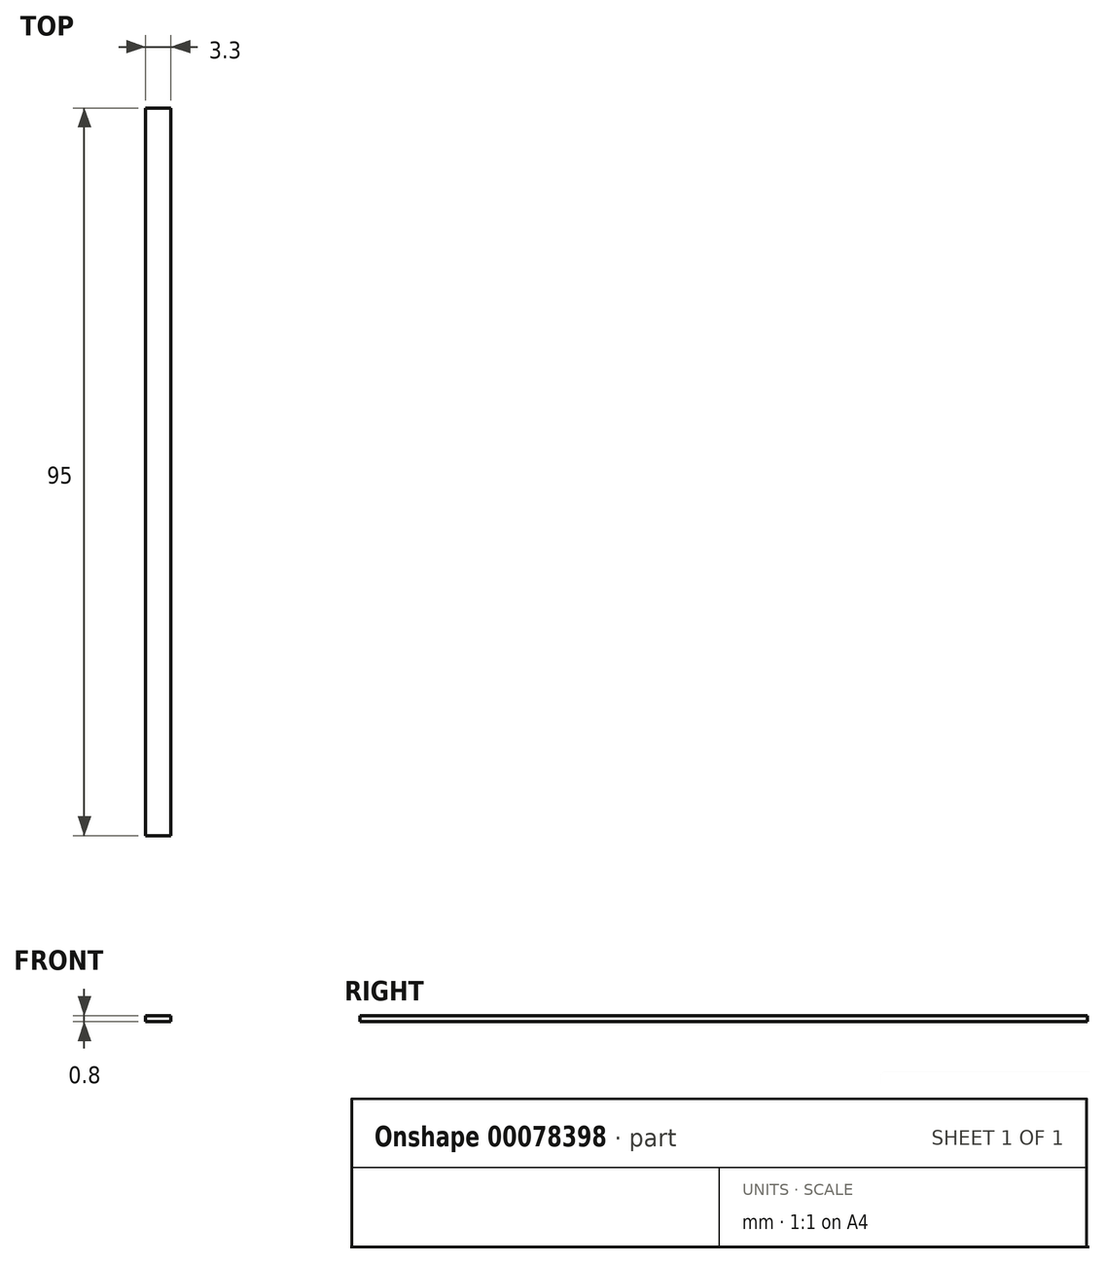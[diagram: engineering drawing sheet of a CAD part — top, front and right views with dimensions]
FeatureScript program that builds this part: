
annotation { "Feature Type Name" : "Feature", "Feature Type Description" : "" }
export const myFeature = defineFeature(function(context is Context, id is Id, definition is map)
    precondition{}
    {
        {
            var Q0;
            Q0=qCreatedBy(makeId("Top.planeOp"),FACE);
            var sketch = newSketch(context, id + "F0", { "sketchPlane" : qUnion([Q0])});
            skLineSegment(sketch, "E0.bottom", {"start": v(-1.65, 47.5) * mm, "end": v(1.65, 47.5) * mm});
            skLineSegment(sketch, "E0.top", {"start": v(-1.65, -47.5) * mm, "end": v(1.65, -47.5) * mm});
            skLineSegment(sketch, "E0.left", {"start": v(-1.65, 47.5) * mm, "end": v(-1.65, -47.5) * mm});
            skLineSegment(sketch, "E0.right", {"start": v(1.65, 47.5) * mm, "end": v(1.65, -47.5) * mm});
            skPoint(sketch, "E0.middle", {"position": v(0, 0) * mm});
            skSolve(sketch);
        }
        {
            var Q0;
            Q0=makeQuery(id+"F0.imprint","IMPRINT",FACE,{"disambiguationData":[TD([[makeQuery(id+"F0.imprint","IMPRINT",EDGE,{"derivedFrom":sQuery(id+"F0.wireOp",EDGE,"E0.bottom")}),-1.0]])]});
            extrude(context, id + "F1", {"entities" : qUnion([Q0]), "depth" : 0.8 * mm, "offsetDistance" : 25 * mm});
        }
    });
